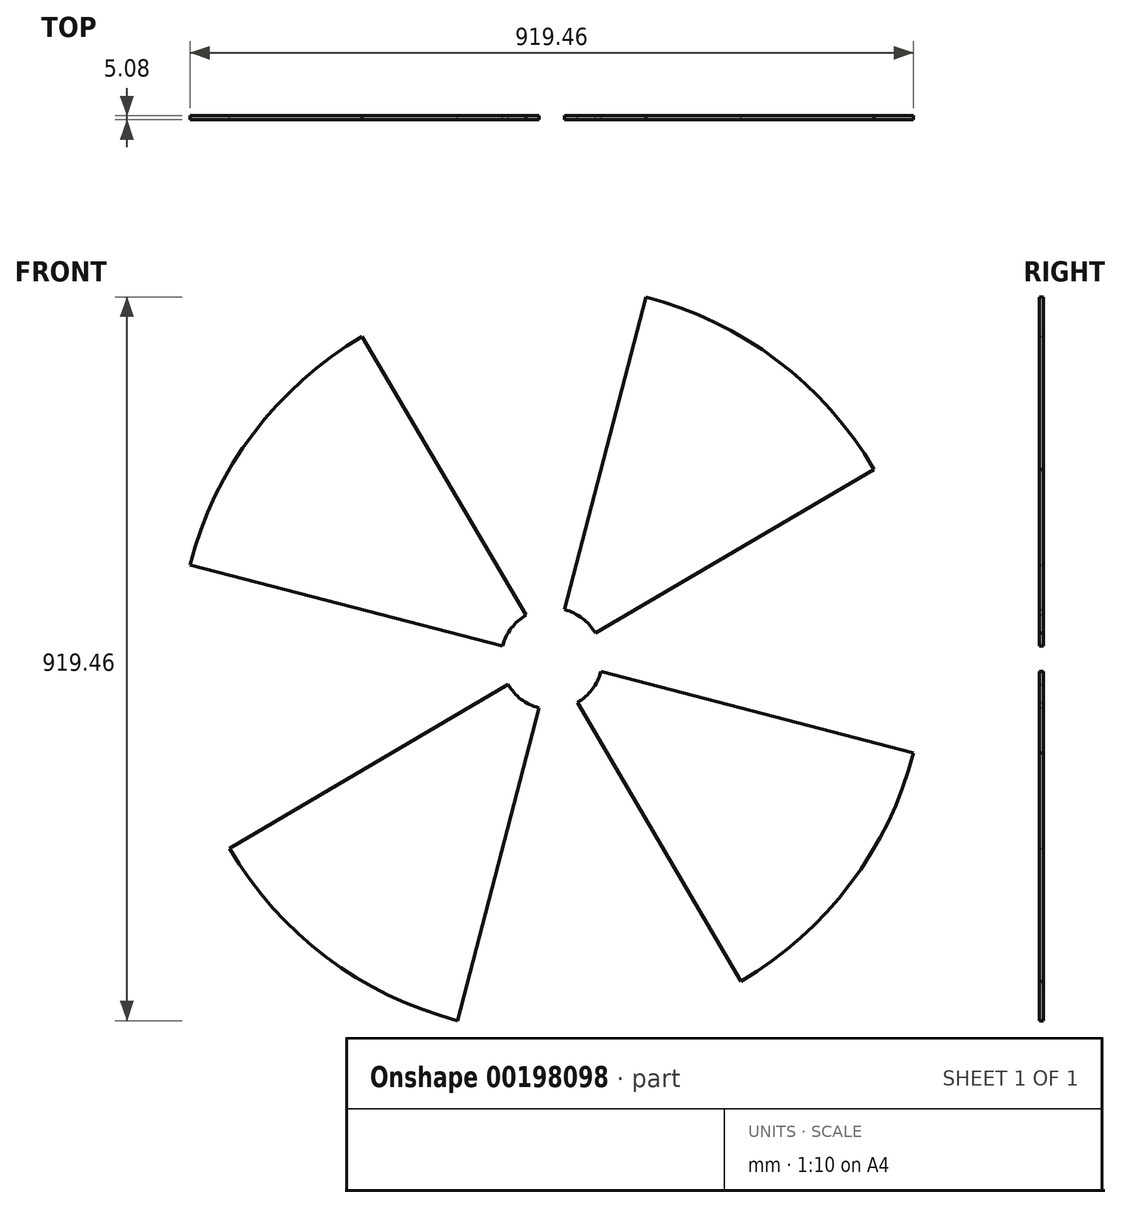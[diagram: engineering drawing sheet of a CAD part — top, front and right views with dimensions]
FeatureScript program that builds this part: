
annotation { "Feature Type Name" : "Feature", "Feature Type Description" : "" }
export const myFeature = defineFeature(function(context is Context, id is Id, definition is map)
    precondition{}
    {
        {
            var Q0;
            Q0=qCreatedBy(makeId("Front.planeOp"),FACE);
            var sketch = newSketch(context, id + "F0", { "sketchPlane" : qUnion([Q0])});
            skCircle(sketch, "E0", {"center": v(0, 0) * mm, "radius": 474.98 * mm});
            skLineSegment(sketch, "E1", {"start": v(-240.64, 409.5) * mm, "end": v(-32.66, 55.58) * mm});
            skLineSegment(sketch, "E2", {"start": v(-459.73, 119.4) * mm, "end": v(-62.4, 16.2) * mm});
            skLineSegment(sketch, "E3", {"start": v(409.5, 240.64) * mm, "end": v(55.58, 32.66) * mm});
            skLineSegment(sketch, "E4", {"start": v(119.4, 459.73) * mm, "end": v(16.2, 62.4) * mm});
            skLineSegment(sketch, "E5.trimOffspring", {"start": v(62.4, -16.2) * mm, "end": v(459.73, -119.4) * mm});
            skLineSegment(sketch, "E6", {"start": v(32.66, -55.58) * mm, "end": v(240.64, -409.5) * mm});
            skLineSegment(sketch, "E7", {"start": v(0, 0) * mm, "end": v(-0.46, -1.78) * mm});
            skArc(sketch, "E8", {"start": v(55.58, 32.66) * mm, "mid": v(-32.66, 55.58) * mm, "end": v(-55.58, -32.66) * mm});
            skArc(sketch, "E9", {"start": v(62.4, -16.2) * mm, "mid": v(63.84, 8.9) * mm, "end": v(55.58, 32.66) * mm});
            skArc(sketch, "E10", {"start": v(32.66, -55.58) * mm, "mid": v(51.44, -38.85) * mm, "end": v(62.4, -16.2) * mm});
            skLineSegment(sketch, "E11", {"start": v(-16.2, -62.4) * mm, "end": v(-16.2, -62.4) * mm});
            skArc(sketch, "E12", {"start": v(-55.58, -32.66) * mm, "mid": v(-16.2, -62.4) * mm, "end": v(32.66, -55.58) * mm});
            skLineSegment(sketch, "E13.trimOffspring", {"start": v(-55.58, -32.66) * mm, "end": v(-409.5, -240.64) * mm});
            skLineSegment(sketch, "E14", {"start": v(-16.2, -62.4) * mm, "end": v(-119.4, -459.73) * mm});
            skSolve(sketch);
        }
        {
            var Q0;
            Q0=qCreatedBy(makeId("Right.planeOp"),FACE);
            var sketch = newSketch(context, id + "F1", { "sketchPlane" : qUnion([Q0])});
            skLineSegment(sketch, "E15", {"start": v(0, 0) * mm, "end": v(0, -474.98) * mm});
            skCircle(sketch, "E16", {"center": v(0, -474.98) * mm, "radius": 6.35 * mm});
            skCircle(sketch, "E17", {"center": v(0, -64.46) * mm, "radius": 6.35 * mm});
            skSolve(sketch);
        }
        {
            var Q0;
            Q0=sQuery(id+"F0.wireOp",EDGE,"E2");
            cPlane(context, id + "F2", {"entities" : qUnion([Q0]), "cplaneType" : CPlaneType.MID_PLANE, "offset" : 25.4 * mm, "width" : 152.4 * mm, "height" : 152.4 * mm});
        }
        {
            var Q0;
            {var subQ0=sQuery(id+"F0.wireOp",EDGE,"E3");Q0=makeQuery(id+"F0.imprint","IMPRINT",FACE,{"disambiguationData":[TD([[makeQuery(id+"F0.imprint","IMPRINT",EDGE,{"derivedFrom":subQ0}),-1.0]])]});}
            var Q1;
            {var subQ0=sQuery(id+"F0.wireOp",EDGE,"E1");Q1=makeQuery(id+"F0.imprint","IMPRINT",FACE,{"disambiguationData":[TD([[makeQuery(id+"F0.imprint","IMPRINT",EDGE,{"derivedFrom":subQ0}),-1.0]])]});}
            var Q2;
            {var subQ0=sQuery(id+"F0.wireOp",EDGE,"E13.trimOffspring");Q2=makeQuery(id+"F0.imprint","IMPRINT",FACE,{"disambiguationData":[TD([[makeQuery(id+"F0.imprint","IMPRINT",EDGE,{"derivedFrom":subQ0}),1.0]])]});}
            var Q3;
            {var subQ0=sQuery(id+"F0.wireOp",EDGE,"E5.trimOffspring");Q3=makeQuery(id+"F0.imprint","IMPRINT",FACE,{"disambiguationData":[TD([[makeQuery(id+"F0.imprint","IMPRINT",EDGE,{"derivedFrom":subQ0}),-1.0]])]});}
            extrude(context, id + "F3", {"entities" : qUnion([Q0, Q1, Q2, Q3]), "endBound" : BoundingType.SYMMETRIC, "depth" : 5.08 * mm});
        }
    });
